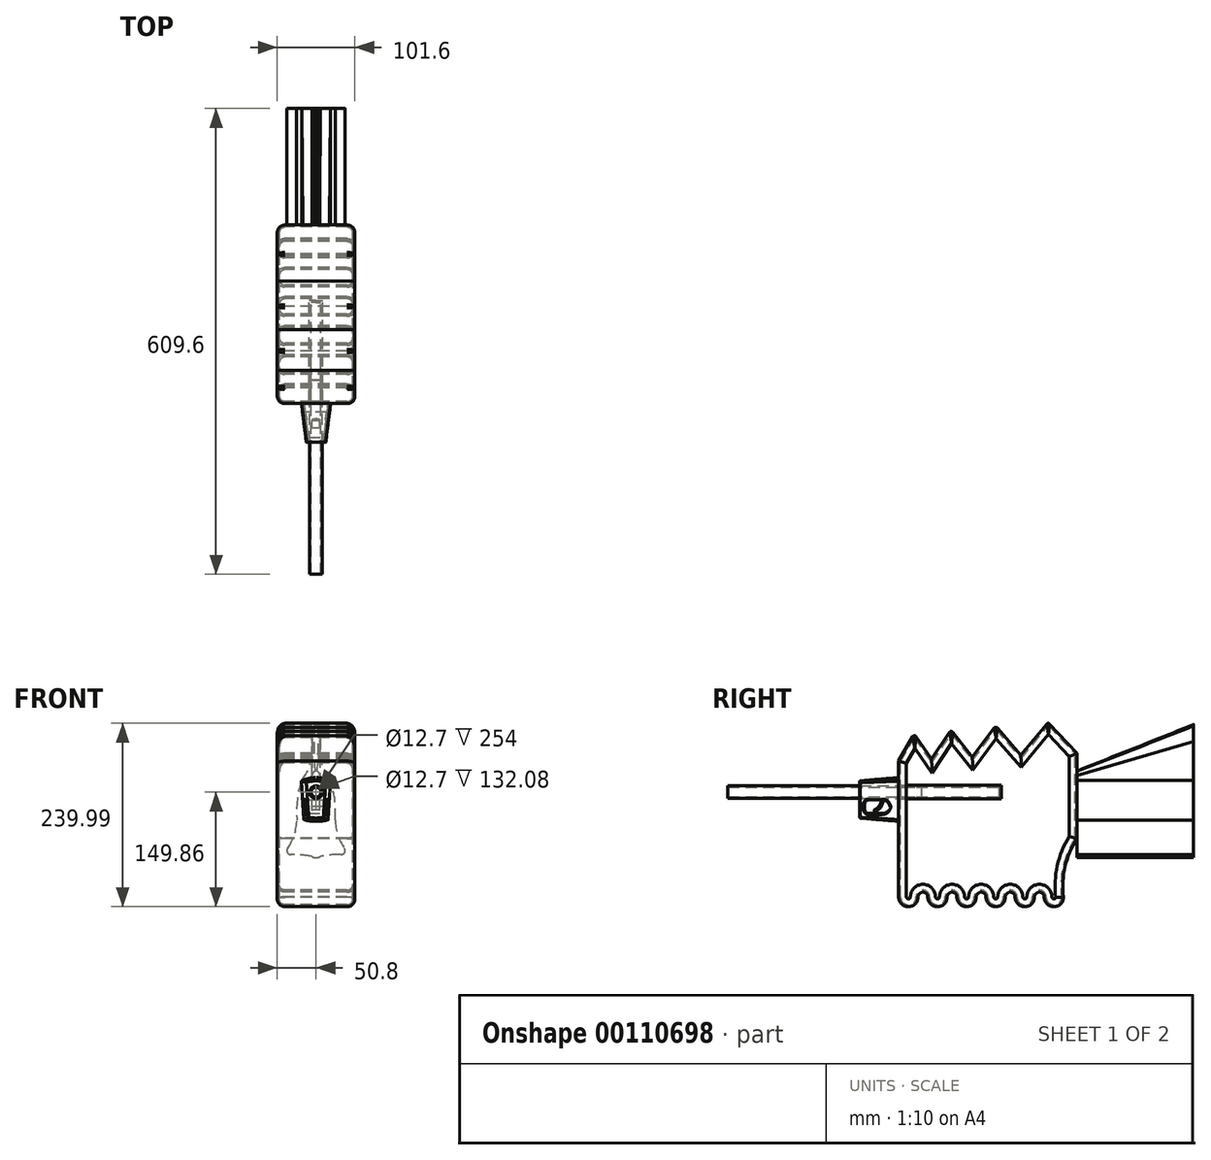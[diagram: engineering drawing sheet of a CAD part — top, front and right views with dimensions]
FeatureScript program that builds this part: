
annotation { "Feature Type Name" : "Feature", "Feature Type Description" : "" }
export const myFeature = defineFeature(function(context is Context, id is Id, definition is map)
    precondition{}
    {
        {
            var Q0;
            Q0=qCreatedBy(makeId("Front.planeOp"),FACE);
            cPlane(context, id + "F0", {"entities" : qUnion([Q0]), "cplaneType" : CPlaneType.OFFSET, "offset" : 101.6 * mm, "width" : 152.4 * mm, "height" : 152.4 * mm});
        }
        {
            var Q0;
            Q0=qCreatedBy(makeId("Front.planeOp"),FACE);
            cPlane(context, id + "F1", {"entities" : qUnion([Q0]), "cplaneType" : CPlaneType.OFFSET, "offset" : 101.6 * mm, "oppositeDirection" : true, "width" : 152.4 * mm, "height" : 152.4 * mm});
        }
        {
            var Q0;
            Q0=qCreatedBy(id+"F0.planeOp",FACE);
            var sketch = newSketch(context, id + "F2", { "sketchPlane" : qUnion([Q0])});
            skCircle(sketch, "E0", {"center": v(0, 25.4) * mm, "radius": 6.35 * mm});
            skCircle(sketch, "E1", {"center": v(0, 25.4) * mm, "radius": 8.26 * mm});
            skSolve(sketch);
        }
        {
            var Q0;
            Q0=makeQuery(id+"F2.imprint","IMPRINT",FACE,{"disambiguationData":[TD([[makeQuery(id+"F2.imprint","IMPRINT",EDGE,{"derivedFrom":sQuery(id+"F2.wireOp",EDGE,"E0")}),-1.0]])]});
            extrude(context, id + "F3", {"entities" : qUnion([Q0]), "depth" : 254 * mm});
        }
        {
            var Q0;
            Q0=qCreatedBy(id+"F1.planeOp",FACE);
            var sketch = newSketch(context, id + "F4", { "sketchPlane" : qUnion([Q0])});
            skEllipse(sketch, "E2", {"center": v(0, 0) * mm, "majorRadius": 60.33 * mm, "minorRadius": 25.4 * mm, "majorAxis": v(0, 1)});
            skSolve(sketch);
        }
        {
            var Q0;
            Q0 = qSketchRegion(id + "F4", true);
            extrude(context, id + "F5", {"entities" : qUnion([Q0]), "oppositeDirection" : true, "depth" : 152.4 * mm});
        }
        {
            var Q0;
            Q0=qCreatedBy(id+"F1.planeOp",FACE);
            var sketch = newSketch(context, id + "F6", { "sketchPlane" : qUnion([Q0])});
            skLineSegment(sketch, "E3.bottom", {"start": v(27.37, 66.04) * mm, "end": v(-29.78, 66.04) * mm});
            skLineSegment(sketch, "E3.top", {"start": v(27.37, 40.64) * mm, "end": v(-29.78, 40.64) * mm});
            skLineSegment(sketch, "E3.left", {"start": v(27.37, 66.04) * mm, "end": v(27.37, 40.64) * mm});
            skLineSegment(sketch, "E3.right", {"start": v(-29.78, 66.04) * mm, "end": v(-29.78, 40.64) * mm});
            skSolve(sketch);
        }
        {
            var Q0;
            Q0 = qSketchRegion(id + "F6", true);
            extrude(context, id + "F7", {"entities" : qUnion([Q0]), "operationType" : NewBodyOperationType.REMOVE, "oppositeDirection" : true, "depth" : 152.4 * mm});
        }
        {
            var Q0;
            Q0=qCreatedBy(id+"F1.planeOp",FACE);
            var sketch = newSketch(context, id + "F8", { "sketchPlane" : qUnion([Q0])});
            skArc(sketch, "E4", {"start": v(5.08, 47) * mm, "mid": v(11.16, 42.16) * mm, "end": v(18.77, 40.64) * mm});
            skArc(sketch, "E5", {"start": v(5.08, 47) * mm, "mid": v(3.67, 51.07) * mm, "end": v(0, 53.34) * mm});
            skArc(sketch, "E6.MirrorCS", {"start": v(-5.08, 47) * mm, "mid": v(-3.67, 51.07) * mm, "end": v(0, 53.34) * mm});
            skArc(sketch, "E7.MirrorCS", {"start": v(-5.08, 47) * mm, "mid": v(-11.16, 42.16) * mm, "end": v(-18.77, 40.64) * mm});
            skLineSegment(sketch, "E8", {"start": v(18.77, 40.64) * mm, "end": v(-18.77, 40.64) * mm});
            skSolve(sketch);
        }
        {
            var Q0;
            Q0=qCreatedBy(makeId("Front.planeOp"),FACE);
            cPlane(context, id + "F9", {"entities" : qUnion([Q0]), "cplaneType" : CPlaneType.OFFSET, "offset" : 254 * mm, "oppositeDirection" : true, "width" : 152.4 * mm, "height" : 152.4 * mm});
        }
        {
            var Q0;
            Q0=qCreatedBy(id+"F9.planeOp",FACE);
            var sketch = newSketch(context, id + "F10", { "sketchPlane" : qUnion([Q0])});
            skArc(sketch, "E9", {"start": v(-18.77, 40.64) * mm, "mid": v(-6.96, 64.7) * mm, "end": v(-5.08, 91.44) * mm});
            skArc(sketch, "E10", {"start": v(0, 116.84) * mm, "mid": v(-4.76, 104.58) * mm, "end": v(-5.08, 91.44) * mm});
            skArc(sketch, "E11.MirrorCS", {"start": v(18.77, 40.64) * mm, "mid": v(6.96, 64.7) * mm, "end": v(5.08, 91.44) * mm});
            skArc(sketch, "E12.MirrorCS", {"start": v(0, 116.84) * mm, "mid": v(4.76, 104.58) * mm, "end": v(5.08, 91.44) * mm});
            skLineSegment(sketch, "E13", {"start": v(18.77, 40.64) * mm, "end": v(-18.77, 40.64) * mm});
            skSolve(sketch);
        }
        {
            var Q1;
            Q1=makeQuery(id+"F10.imprint","IMPRINT",FACE,{"disambiguationData":[TD([[makeQuery(id+"F10.imprint","IMPRINT",EDGE,{"derivedFrom":sQuery(id+"F10.wireOp",EDGE,"E9")}),-1.0]])]});
            var Q2;
            {var subQ4=sQuery(id+"F8.wireOp",EDGE,"E5");Q2=makeQuery(id+"F8.imprint","IMPRINT",FACE,{"disambiguationData":[TD([[makeQuery(id+"F8.imprint","IMPRINT",EDGE,{"derivedFrom":subQ4}),1.0]])]});}
            loft(context, id + "F11", {"operationType" : NewBodyOperationType.ADD, "sheetProfilesArray" : [{ "sheetProfileEntities" : qUnion([Q1]) }, { "sheetProfileEntities" : qUnion([Q2]) }]});
        }
        {
            var Q0;
            Q0=makeQuery(id+"F11.opLoft","SWEPT_EDGE",EDGE,{"disambiguationData":[OSD([sQuery(id+"F8.wireOp",EDGE,"E5"),sQuery(id+"F8.wireOp",EDGE,"E6.MirrorCS"),sQuery(id+"F10.wireOp",EDGE,"E10"),sQuery(id+"F10.wireOp",EDGE,"E12.MirrorCS")])]});
            fillet(context, id + "F12", {"entities" : qUnion([Q0]), "radius" : 2.54 * mm, "tangentPropagation" : true, "allowEdgeOverflow" : false});
        }
        {
            var Q0;
            Q0=qCreatedBy(id+"F1.planeOp",FACE);
            var sketch = newSketch(context, id + "F13", { "sketchPlane" : qUnion([Q0])});
            skArc(sketch, "E14", {"start": v(25.4, 0) * mm, "mid": v(28.58, -30.69) * mm, "end": v(44.45, -57.15) * mm});
            skArc(sketch, "E15", {"start": v(44.45, -57.15) * mm, "mid": v(22.06, -56.37) * mm, "end": v(0, -60.33) * mm});
            skLineSegment(sketch, "E16", {"start": v(25.4, 0) * mm, "end": v(0, -60.32) * mm});
            skArc(sketch, "E17.MirrorCS", {"start": v(-44.45, -57.15) * mm, "mid": v(-22.06, -56.37) * mm, "end": v(0, -60.33) * mm});
            skArc(sketch, "E18.MirrorCS", {"start": v(-25.4, 0) * mm, "mid": v(-28.58, -30.69) * mm, "end": v(-44.45, -57.15) * mm});
            skLineSegment(sketch, "E19.MirrorCS", {"start": v(-25.4, 0) * mm, "end": v(0, -60.33) * mm});
            skSolve(sketch);
        }
        {
            var Q0;
            Q0 = qSketchRegion(id + "F13", true);
            extrude(context, id + "F14", {"entities" : qUnion([Q0]), "operationType" : NewBodyOperationType.ADD, "oppositeDirection" : true, "depth" : 152.4 * mm});
        }
        {
            var Q0;
            Q0=makeQuery(id+"F14.opExtrude","SWEPT_EDGE",EDGE,{"disambiguationData":[OSD([sQuery(id+"F13.wireOp",EDGE,"E14"),sQuery(id+"F13.wireOp",EDGE,"E15")])]});
            var Q1;
            Q1=makeQuery(id+"F14.opExtrude","SWEPT_EDGE",EDGE,{"disambiguationData":[OSD([sQuery(id+"F13.wireOp",EDGE,"E17.MirrorCS"),sQuery(id+"F13.wireOp",EDGE,"E18.MirrorCS")])]});
            fillet(context, id + "F15", {"entities" : qUnion([Q0, Q1]), "radius" : 5.08 * mm, "tangentPropagation" : true, "allowEdgeOverflow" : false});
        }
        {
            var Q0;
            Q0=qCreatedBy(makeId("Right.planeOp"),FACE);
            var sketch = newSketch(context, id + "F16", { "sketchPlane" : qUnion([Q0])});
            skLineSegment(sketch, "E20", {"start": v(101.6, 76.2) * mm, "end": v(63.5, 116.84) * mm});
            skLineSegment(sketch, "E21", {"start": v(63.5, 116.84) * mm, "end": v(27.94, 73.66) * mm});
            skLineSegment(sketch, "E22", {"start": v(-35.56, 71.12) * mm, "end": v(-63.5, 106.68) * mm});
            skLineSegment(sketch, "E23", {"start": v(-63.5, 106.68) * mm, "end": v(-88.9, 68.58) * mm});
            skLineSegment(sketch, "E24", {"start": v(-132.08, 66.04) * mm, "end": v(-132.08, -111.76) * mm});
            skLineSegment(sketch, "E25", {"start": v(27.94, 73.66) * mm, "end": v(-5.08, 111.76) * mm});
            skLineSegment(sketch, "E26", {"start": v(-5.08, 111.76) * mm, "end": v(-35.56, 71.12) * mm});
            skLineSegment(sketch, "E27", {"start": v(-88.9, 68.58) * mm, "end": v(-111.76, 101.6) * mm});
            skLineSegment(sketch, "E28", {"start": v(-111.76, 101.6) * mm, "end": v(-132.08, 66.04) * mm});
            skArc(sketch, "E29", {"start": v(-132.08, -111.76) * mm, "mid": v(-119.38, -124.46) * mm, "end": v(-106.68, -111.76) * mm});
            skArc(sketch, "E30", {"start": v(-106.68, -111.76) * mm, "mid": v(-100.33, -105.4) * mm, "end": v(-93.98, -111.76) * mm});
            skArc(sketch, "E31", {"start": v(-93.98, -111.76) * mm, "mid": v(-81.28, -124.46) * mm, "end": v(-68.58, -111.76) * mm});
            skArc(sketch, "E32", {"start": v(-68.58, -111.76) * mm, "mid": v(-62.23, -105.4) * mm, "end": v(-55.88, -111.76) * mm});
            skArc(sketch, "E33", {"start": v(-55.88, -111.76) * mm, "mid": v(-43.18, -124.46) * mm, "end": v(-30.48, -111.76) * mm});
            skArc(sketch, "E34", {"start": v(-30.48, -111.76) * mm, "mid": v(-24.13, -105.4) * mm, "end": v(-17.78, -111.76) * mm});
            skArc(sketch, "E35", {"start": v(-17.78, -111.76) * mm, "mid": v(-5.08, -124.46) * mm, "end": v(7.62, -111.76) * mm});
            skArc(sketch, "E36", {"start": v(7.62, -111.76) * mm, "mid": v(13.97, -105.41) * mm, "end": v(20.32, -111.76) * mm});
            skArc(sketch, "E37", {"start": v(20.32, -111.76) * mm, "mid": v(33.02, -124.46) * mm, "end": v(45.72, -111.76) * mm});
            skArc(sketch, "E38", {"start": v(45.72, -111.76) * mm, "mid": v(52.07, -105.4) * mm, "end": v(58.42, -111.76) * mm});
            skArc(sketch, "E39", {"start": v(58.42, -111.76) * mm, "mid": v(71.12, -124.46) * mm, "end": v(83.82, -111.76) * mm});
            skArc(sketch, "E40", {"start": v(101.6, -35.56) * mm, "mid": v(85.65, -72.01) * mm, "end": v(83.82, -111.76) * mm});
            skLineSegment(sketch, "E41", {"start": v(101.6, 76.2) * mm, "end": v(101.6, -35.56) * mm});
            skSolve(sketch);
        }
        {
            var Q0;
            Q0=makeQuery(id+"F16.imprint","IMPRINT",FACE,{"disambiguationData":[TD([[makeQuery(id+"F16.imprint","IMPRINT",EDGE,{"derivedFrom":sQuery(id+"F16.wireOp",EDGE,"E20")}),1.0]])]});
            extrude(context, id + "F17", {"entities" : qUnion([Q0]), "depth" : 50.8 * mm, "hasSecondDirection" : true, "secondDirectionOppositeDirection" : true, "secondDirectionDepth" : 50.8 * mm});
        }
        {
            var Q0;
            Q0=makeQuery(id+"F17.opExtrude","SWEPT_EDGE",EDGE,{"disambiguationData":[OSD([sQuery(id+"F16.wireOp",EDGE,"E27"),sQuery(id+"F16.wireOp",EDGE,"E28")])]});
            var Q1;
            Q1=makeQuery(id+"F17.opExtrude","SWEPT_EDGE",EDGE,{"disambiguationData":[OSD([sQuery(id+"F16.wireOp",EDGE,"E22"),sQuery(id+"F16.wireOp",EDGE,"E23")])]});
            var Q2;
            Q2=makeQuery(id+"F17.opExtrude","SWEPT_EDGE",EDGE,{"disambiguationData":[OSD([sQuery(id+"F16.wireOp",EDGE,"E25"),sQuery(id+"F16.wireOp",EDGE,"E26")])]});
            var Q3;
            Q3=makeQuery(id+"F17.opExtrude","SWEPT_EDGE",EDGE,{"disambiguationData":[OSD([sQuery(id+"F16.wireOp",EDGE,"E20"),sQuery(id+"F16.wireOp",EDGE,"E21")])]});
            fillet(context, id + "F18", {"entities" : qUnion([Q0, Q1, Q2, Q3]), "radius" : 2.54 * mm, "tangentPropagation" : true, "allowEdgeOverflow" : false});
        }
        {
            var Q0;
            Q0=makeQuery(id+"F17.opExtrude","CAP_FACE",FACE,{"disambiguationData":[OSD([sQuery(id+"F16.wireOp",EDGE,"E20"),sQuery(id+"F16.wireOp",EDGE,"E21"),sQuery(id+"F16.wireOp",EDGE,"E22"),sQuery(id+"F16.wireOp",EDGE,"E23"),sQuery(id+"F16.wireOp",EDGE,"E24"),sQuery(id+"F16.wireOp",EDGE,"E25"),sQuery(id+"F16.wireOp",EDGE,"E26"),sQuery(id+"F16.wireOp",EDGE,"E27"),sQuery(id+"F16.wireOp",EDGE,"E28"),sQuery(id+"F16.wireOp",EDGE,"E29"),sQuery(id+"F16.wireOp",EDGE,"E30"),sQuery(id+"F16.wireOp",EDGE,"E31"),sQuery(id+"F16.wireOp",EDGE,"E32"),sQuery(id+"F16.wireOp",EDGE,"E33"),sQuery(id+"F16.wireOp",EDGE,"E34"),sQuery(id+"F16.wireOp",EDGE,"E35"),sQuery(id+"F16.wireOp",EDGE,"E36"),sQuery(id+"F16.wireOp",EDGE,"E37"),sQuery(id+"F16.wireOp",EDGE,"E38"),sQuery(id+"F16.wireOp",EDGE,"E39"),sQuery(id+"F16.wireOp",EDGE,"E40"),sQuery(id+"F16.wireOp",EDGE,"E41")])],"isStart":false});
            fillet(context, id + "F19", {"entities" : qUnion([Q0]), "radius" : 10.16 * mm, "tangentPropagation" : true, "allowEdgeOverflow" : false});
        }
        {
            var Q0;
            Q0=makeQuery(id+"F17.opExtrude","CAP_FACE",FACE,{"disambiguationData":[OSD([sQuery(id+"F16.wireOp",EDGE,"E20"),sQuery(id+"F16.wireOp",EDGE,"E21"),sQuery(id+"F16.wireOp",EDGE,"E22"),sQuery(id+"F16.wireOp",EDGE,"E23"),sQuery(id+"F16.wireOp",EDGE,"E24"),sQuery(id+"F16.wireOp",EDGE,"E25"),sQuery(id+"F16.wireOp",EDGE,"E26"),sQuery(id+"F16.wireOp",EDGE,"E27"),sQuery(id+"F16.wireOp",EDGE,"E28"),sQuery(id+"F16.wireOp",EDGE,"E29"),sQuery(id+"F16.wireOp",EDGE,"E30"),sQuery(id+"F16.wireOp",EDGE,"E31"),sQuery(id+"F16.wireOp",EDGE,"E32"),sQuery(id+"F16.wireOp",EDGE,"E33"),sQuery(id+"F16.wireOp",EDGE,"E34"),sQuery(id+"F16.wireOp",EDGE,"E35"),sQuery(id+"F16.wireOp",EDGE,"E36"),sQuery(id+"F16.wireOp",EDGE,"E37"),sQuery(id+"F16.wireOp",EDGE,"E38"),sQuery(id+"F16.wireOp",EDGE,"E39"),sQuery(id+"F16.wireOp",EDGE,"E40"),sQuery(id+"F16.wireOp",EDGE,"E41")])],"isStart":true});
            fillet(context, id + "F20", {"entities" : qUnion([Q0]), "radius" : 10.16 * mm, "tangentPropagation" : true, "allowEdgeOverflow" : false});
        }
        {
            var Q0;
            Q0=qCreatedBy(makeId("Front.planeOp"),FACE);
            var sketch = newSketch(context, id + "F21", { "sketchPlane" : qUnion([Q0])});
            skCircle(sketch, "E42", {"center": v(0, 25.4) * mm, "radius": 6.35 * mm});
            skSolve(sketch);
        }
        {
            var Q0;
            Q0 = qSketchRegion(id + "F21", true);
            extrude(context, id + "F22", {"entities" : qUnion([Q0]), "operationType" : NewBodyOperationType.REMOVE, "endBound" : BoundingType.THROUGH_ALL, "depth" : 25.4 * mm});
        }
        {
            var Q0;
            Q0=makeQuery(id+"F17.opExtrude","CAP_FACE",FACE,{"disambiguationData":[OSD([sQuery(id+"F16.wireOp",EDGE,"E20"),sQuery(id+"F16.wireOp",EDGE,"E21"),sQuery(id+"F16.wireOp",EDGE,"E22"),sQuery(id+"F16.wireOp",EDGE,"E23"),sQuery(id+"F16.wireOp",EDGE,"E24"),sQuery(id+"F16.wireOp",EDGE,"E25"),sQuery(id+"F16.wireOp",EDGE,"E26"),sQuery(id+"F16.wireOp",EDGE,"E27"),sQuery(id+"F16.wireOp",EDGE,"E28"),sQuery(id+"F16.wireOp",EDGE,"E29"),sQuery(id+"F16.wireOp",EDGE,"E30"),sQuery(id+"F16.wireOp",EDGE,"E31"),sQuery(id+"F16.wireOp",EDGE,"E32"),sQuery(id+"F16.wireOp",EDGE,"E33"),sQuery(id+"F16.wireOp",EDGE,"E34"),sQuery(id+"F16.wireOp",EDGE,"E35"),sQuery(id+"F16.wireOp",EDGE,"E36"),sQuery(id+"F16.wireOp",EDGE,"E37"),sQuery(id+"F16.wireOp",EDGE,"E38"),sQuery(id+"F16.wireOp",EDGE,"E39"),sQuery(id+"F16.wireOp",EDGE,"E40"),sQuery(id+"F16.wireOp",EDGE,"E41")])],"isStart":false});
            shell(context, id + "F23", {"entities" : qUnion([Q0]), "thickness" : 2.54 * mm});
        }
        {
            var Q0;
            Q0=makeQuery(id+"F17.opExtrude","SWEPT_FACE",FACE,{"disambiguationData":[OSD([sQuery(id+"F16.wireOp",EDGE,"E24")])]});
            var sketch = newSketch(context, id + "F24", { "sketchPlane" : qUnion([Q0])});
            skArc(sketch, "E43", {"start": v(19.05, 40.16) * mm, "mid": v(0, 44.45) * mm, "end": v(-19.05, 40.16) * mm});
            skArc(sketch, "E44", {"start": v(-15.88, -10.68) * mm, "mid": v(0, -12.7) * mm, "end": v(15.87, -10.68) * mm});
            skLineSegment(sketch, "E45", {"start": v(-15.88, -10.68) * mm, "end": v(-19.05, 40.16) * mm});
            skLineSegment(sketch, "E46", {"start": v(19.05, 40.16) * mm, "end": v(15.88, -10.68) * mm});
            skSolve(sketch);
        }
        {
            var Q0;
            Q0=makeQuery(id+"F24.imprint","IMPRINT",FACE,{"disambiguationData":[TD([[makeQuery(id+"F24.imprint","IMPRINT",EDGE,{"derivedFrom":sQuery(id+"F24.wireOp",EDGE,"E43")}),-1.0]])]});
            cPlane(context, id + "F25", {"entities" : qUnion([Q0]), "cplaneType" : CPlaneType.OFFSET, "offset" : 50.8 * mm, "width" : 152.4 * mm, "height" : 152.4 * mm});
        }
        {
            var Q0;
            Q0=qCreatedBy(id+"F25.planeOp",FACE);
            var sketch = newSketch(context, id + "F26", { "sketchPlane" : qUnion([Q0])});
            skArc(sketch, "E47", {"start": v(12.7, 38.1) * mm, "mid": v(0, 40.16) * mm, "end": v(-12.7, 38.1) * mm});
            skArc(sketch, "E48", {"start": v(-9.53, -7.62) * mm, "mid": v(0, -8.34) * mm, "end": v(9.52, -7.62) * mm});
            skLineSegment(sketch, "E49", {"start": v(-9.53, -7.62) * mm, "end": v(-12.7, 38.1) * mm});
            skLineSegment(sketch, "E50", {"start": v(12.7, 38.1) * mm, "end": v(9.53, -7.62) * mm});
            skSolve(sketch);
        }
        {
            var Q0;
            Q0 = qSketchRegion(id + "F24", true);
            var Q1;
            Q1 = qSketchRegion(id + "F26", true);
            loft(context, id + "F27", {"sheetProfilesArray" : [{ "sheetProfileEntities" : qUnion([Q0]) }, { "sheetProfileEntities" : qUnion([Q1]) }]});
        }
        {
            var Q0;
            Q0=makeQuery(id+"F27.opLoft","SWEPT_EDGE",EDGE,{"disambiguationData":[OSD([sQuery(id+"F24.wireOp",EDGE,"E43"),sQuery(id+"F24.wireOp",EDGE,"E45"),sQuery(id+"F26.wireOp",EDGE,"E47"),sQuery(id+"F26.wireOp",EDGE,"E49")])]});
            var Q1;
            Q1=makeQuery(id+"F27.opLoft","MID_CAP_EDGE",EDGE,{"disambiguationData":[OSD([sQuery(id+"F26.wireOp",EDGE,"E47"),sQuery(id+"F26.wireOp",EDGE,"E49"),sQuery(id+"F26.wireOp",EDGE,"E50")])],"capPos":1.0});
            var Q2;
            Q2=makeQuery(id+"F27.opLoft","SWEPT_EDGE",EDGE,{"disambiguationData":[OSD([sQuery(id+"F24.wireOp",EDGE,"E43"),sQuery(id+"F24.wireOp",EDGE,"E46"),sQuery(id+"F26.wireOp",EDGE,"E47"),sQuery(id+"F26.wireOp",EDGE,"E50")])]});
            var Q3;
            Q3=makeQuery(id+"F27.opLoft","SWEPT_EDGE",EDGE,{"disambiguationData":[OSD([sQuery(id+"F24.wireOp",EDGE,"E44"),sQuery(id+"F24.wireOp",EDGE,"E46"),sQuery(id+"F26.wireOp",EDGE,"E48"),sQuery(id+"F26.wireOp",EDGE,"E50")])]});
            var Q4;
            Q4=makeQuery(id+"F27.opLoft","SWEPT_EDGE",EDGE,{"disambiguationData":[OSD([sQuery(id+"F24.wireOp",EDGE,"E44"),sQuery(id+"F24.wireOp",EDGE,"E45"),sQuery(id+"F26.wireOp",EDGE,"E48"),sQuery(id+"F26.wireOp",EDGE,"E49")])]});
            var Q5;
            Q5=makeQuery(id+"F27.opLoft","MID_CAP_EDGE",EDGE,{"disambiguationData":[OSD([sQuery(id+"F26.wireOp",EDGE,"E47"),sQuery(id+"F26.wireOp",EDGE,"E48"),sQuery(id+"F26.wireOp",EDGE,"E49")])],"capPos":1.0});
            var Q6;
            Q6=makeQuery(id+"F27.opLoft","MID_CAP_EDGE",EDGE,{"disambiguationData":[OSD([sQuery(id+"F26.wireOp",EDGE,"E48"),sQuery(id+"F26.wireOp",EDGE,"E49"),sQuery(id+"F26.wireOp",EDGE,"E50")])],"capPos":1.0});
            var Q7;
            Q7=makeQuery(id+"F27.opLoft","MID_CAP_EDGE",EDGE,{"disambiguationData":[OSD([sQuery(id+"F26.wireOp",EDGE,"E47"),sQuery(id+"F26.wireOp",EDGE,"E48"),sQuery(id+"F26.wireOp",EDGE,"E50")])],"capPos":1.0});
            fillet(context, id + "F28", {"entities" : qUnion([Q0, Q1, Q2, Q3, Q4, Q5, Q6, Q7]), "radius" : 0.25 * mm, "tangentPropagation" : true, "allowEdgeOverflow" : false});
        }
        {
            var Q0;
            Q0=qCreatedBy(makeId("Right.planeOp"),FACE);
            var sketch = newSketch(context, id + "F29", { "sketchPlane" : qUnion([Q0])});
            skLineSegment(sketch, "E51.bottom", {"start": v(-176.53, 15.24) * mm, "end": v(-143.51, 15.24) * mm});
            skLineSegment(sketch, "E51.top", {"start": v(-176.53, -2.54) * mm, "end": v(-143.51, -2.54) * mm});
            skLineSegment(sketch, "E51.left", {"start": v(-176.53, 15.24) * mm, "end": v(-176.53, -2.54) * mm});
            skLineSegment(sketch, "E51.right", {"start": v(-143.51, 15.24) * mm, "end": v(-143.51, -2.54) * mm});
            skSolve(sketch);
        }
        {
            var Q0;
            Q0 = qSketchRegion(id + "F29", true);
            extrude(context, id + "F30", {"entities" : qUnion([Q0]), "operationType" : NewBodyOperationType.REMOVE, "endBound" : BoundingType.THROUGH_ALL, "oppositeDirection" : true, "depth" : 25.4 * mm, "hasSecondDirection" : true, "secondDirectionBound" : SecondDirectionBoundingType.THROUGH_ALL, "secondDirectionOppositeDirection" : false, "secondDirectionDepth" : 25.4 * mm});
        }
        {
            var Q0;
            Q0=makeQuery(id+"F30.boolean.opBoolean","COPY",EDGE,{"derivedFrom":makeQuery(id+"F30.opExtrude","SWEPT_EDGE",EDGE,{"disambiguationData":[OSD([sQuery(id+"F29.wireOp",EDGE,"E51.bottom"),sQuery(id+"F29.wireOp",EDGE,"E51.left")])]})});
            var Q1;
            Q1=makeQuery(id+"F30.boolean.opBoolean","COPY",EDGE,{"derivedFrom":makeQuery(id+"F30.opExtrude","SWEPT_EDGE",EDGE,{"disambiguationData":[OSD([sQuery(id+"F29.wireOp",EDGE,"E51.top"),sQuery(id+"F29.wireOp",EDGE,"E51.left")])]})});
            fillet(context, id + "F31", {"entities" : qUnion([Q0, Q1]), "radius" : 5.08 * mm, "tangentPropagation" : true, "allowEdgeOverflow" : false});
        }
        {
            var Q0;
            Q0=makeQuery(id+"F30.boolean.opBoolean","COPY",EDGE,{"derivedFrom":makeQuery(id+"F30.opExtrude","SWEPT_EDGE",EDGE,{"disambiguationData":[OSD([sQuery(id+"F29.wireOp",EDGE,"E51.bottom"),sQuery(id+"F29.wireOp",EDGE,"E51.right")])]})});
            var Q1;
            Q1=makeQuery(id+"F30.boolean.opBoolean","COPY",EDGE,{"derivedFrom":makeQuery(id+"F30.opExtrude","SWEPT_EDGE",EDGE,{"disambiguationData":[OSD([sQuery(id+"F29.wireOp",EDGE,"E51.top"),sQuery(id+"F29.wireOp",EDGE,"E51.right")])]})});
            fillet(context, id + "F32", {"entities" : qUnion([Q0, Q1]), "radius" : 10.16 * mm, "tangentPropagation" : true, "allowEdgeOverflow" : false});
        }
        {
            var Q0;
            Q0=makeQuery(id+"F31.opFillet","BLEND_EDGE",EDGE,{"blendedFrom":[makeQuery(id+"F30.boolean.opBoolean","COPY",EDGE,{"derivedFrom":makeQuery(id+"F30.opExtrude","SWEPT_EDGE",EDGE,{"disambiguationData":[OSD([sQuery(id+"F29.wireOp",EDGE,"E51.bottom"),sQuery(id+"F29.wireOp",EDGE,"E51.left")])]})}),makeQuery(id+"F27.opLoft","SWEPT_FACE",FACE,{"disambiguationData":[OSD([sQuery(id+"F24.wireOp",EDGE,"E43"),sQuery(id+"F24.wireOp",EDGE,"E44"),sQuery(id+"F24.wireOp",EDGE,"E46"),sQuery(id+"F26.wireOp",EDGE,"E47"),sQuery(id+"F26.wireOp",EDGE,"E48"),sQuery(id+"F26.wireOp",EDGE,"E50")])]})],"blendedInto":[makeQuery(id+"F27.opLoft","SWEPT_FACE",FACE,{"disambiguationData":[OSD([sQuery(id+"F24.wireOp",EDGE,"E43"),sQuery(id+"F24.wireOp",EDGE,"E44"),sQuery(id+"F24.wireOp",EDGE,"E46"),sQuery(id+"F26.wireOp",EDGE,"E47"),sQuery(id+"F26.wireOp",EDGE,"E48"),sQuery(id+"F26.wireOp",EDGE,"E50")])]})]});
            var Q1;
            Q1=makeQuery(id+"F30.boolean.opBoolean","INTERSECT",EDGE,{"derivedFrom":[makeQuery(id+"F27.opLoft","SWEPT_FACE",FACE,{"disambiguationData":[OSD([sQuery(id+"F24.wireOp",EDGE,"E43"),sQuery(id+"F24.wireOp",EDGE,"E44"),sQuery(id+"F24.wireOp",EDGE,"E45"),sQuery(id+"F26.wireOp",EDGE,"E47"),sQuery(id+"F26.wireOp",EDGE,"E48"),sQuery(id+"F26.wireOp",EDGE,"E49")])]}),makeQuery(id+"F30.opExtrude","SWEPT_FACE",FACE,{"disambiguationData":[OSD([sQuery(id+"F29.wireOp",EDGE,"E51.top")])]})]});
            fillet(context, id + "F33", {"entities" : qUnion([Q0, Q1]), "radius" : 1.27 * mm, "tangentPropagation" : true, "allowEdgeOverflow" : false});
        }
        {
            var Q0;
            Q0=makeQuery(id+"F30.boolean.opBoolean","COPY",FACE,{"derivedFrom":makeQuery(id+"F30.opExtrude","SWEPT_FACE",FACE,{"disambiguationData":[OSD([sQuery(id+"F29.wireOp",EDGE,"E51.bottom")])]})});
            var sketch = newSketch(context, id + "F34", { "sketchPlane" : qUnion([Q0])});
            skEllipse(sketch, "E52", {"center": v(0, 153.67) * mm, "majorRadius": 5.08 * mm, "minorRadius": 1.27 * mm, "majorAxis": v(1, 0)});
            skSolve(sketch);
        }
        {
            var Q0;
            Q0=qCreatedBy(makeId("Right.planeOp"),FACE);
            var sketch = newSketch(context, id + "F35", { "sketchPlane" : qUnion([Q0])});
            skArc(sketch, "E53", {"start": v(-163.83, 1.27) * mm, "mid": v(-156.58, 6.68) * mm, "end": v(-153.67, 15.24) * mm});
            skSolve(sketch);
        }
        {
            var Q0;
            Q0 = qSketchRegion(id + "F34", true);
            var Q1;
            Q1 = qConstructionFilter(qBodyType(qCreatedBy(id + "F35" ,EDGE), BodyType.WIRE), ConstructionObject.NO);
            sweep(context, id + "F36", {"operationType" : NewBodyOperationType.ADD, "profiles" : qUnion([Q0]), "path" : qUnion([Q1])});
        }
    });
